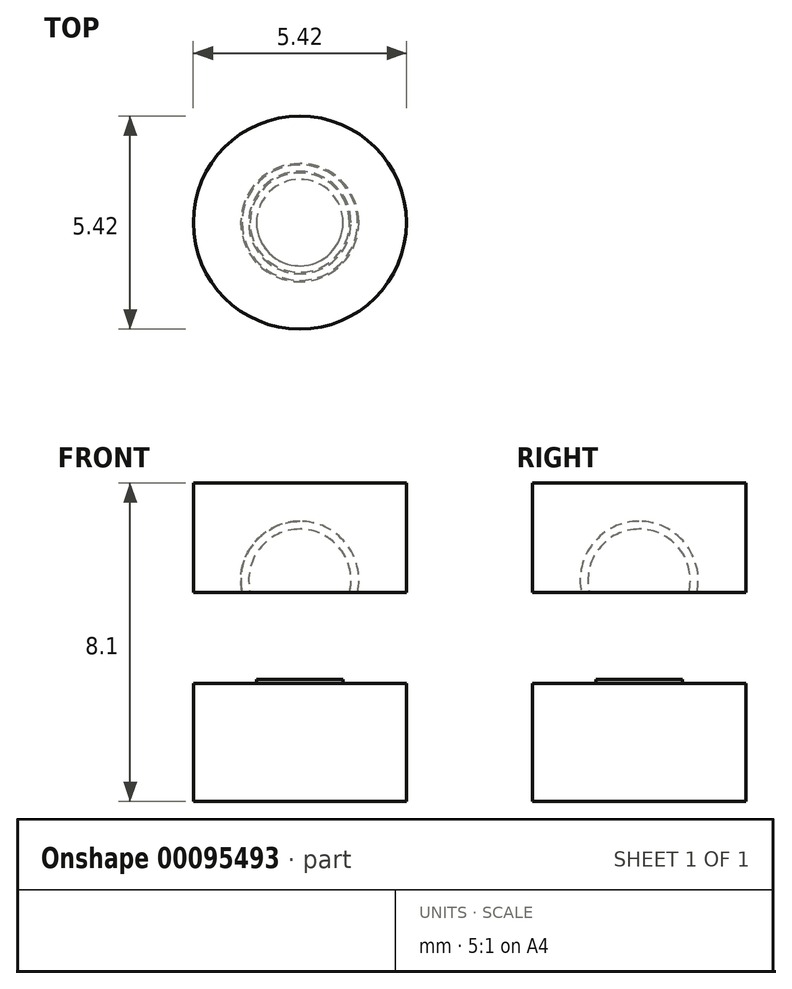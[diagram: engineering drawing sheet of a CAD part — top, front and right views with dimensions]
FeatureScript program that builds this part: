
annotation { "Feature Type Name" : "Feature", "Feature Type Description" : "" }
export const myFeature = defineFeature(function(context is Context, id is Id, definition is map)
    precondition{}
    {
        {
            var Q0;
            Q0=qCreatedBy(makeId("Front.planeOp"),FACE);
            var sketch = newSketch(context, id + "F0", { "sketchPlane" : qUnion([Q0])});
            skArc(sketch, "E0", {"start": v(0, 4.02) * mm, "mid": v(-1.3, 3.27) * mm, "end": v(-1.3, 1.77) * mm});
            skLineSegment(sketch, "E1.bottom", {"start": v(0, 5) * mm, "end": v(-2.7, 5) * mm});
            skLineSegment(sketch, "E1.right", {"start": v(-2.7, 5) * mm, "end": v(-2.7, 0) * mm});
            skPoint(sketch, "E1.middle", {"position": v(0, 0) * mm});
            skLineSegment(sketch, "E2", {"start": v(-1.3, 1.77) * mm, "end": v(-1.3, 0) * mm});
            skPoint(sketch, "E2.endSnap0", {"position": v(2.7, 0) * mm});
            skLineSegment(sketch, "E3", {"start": v(0, 5) * mm, "end": v(0, 4.02) * mm});
            skPoint(sketch, "E4.orphan", {"position": v(2.7, 5) * mm});
            skPoint(sketch, "E5.orphan", {"position": v(2.7, -5) * mm});
            skLineSegment(sketch, "E6", {"start": v(-2.7, 0) * mm, "end": v(-1.3, 0) * mm});
            skPoint(sketch, "E1.top.end.orphan", {"position": v(-2.7, -5) * mm});
            skPoint(sketch, "E1.top.start.orphan", {"position": v(0, -5) * mm});
            skSolve(sketch);
        }
        {
            var Q0;
            Q0=makeQuery(id+"F0.imprint","IMPRINT",FACE,{"disambiguationData":[TD([[makeQuery(id+"F0.imprint","IMPRINT",EDGE,{"derivedFrom":sQuery(id+"F0.wireOp",EDGE,"E0")}),-1.0]])]});
            var Q1;
            Q1=sQuery(id+"F0.wireOp",EDGE,"E3");
            revolve(context, id + "F1", {"entities" : qUnion([Q0]), "axis" : qUnion([Q1]), "revolveType" : RevolveType.FULL});
        }
        {
            var Q0;
            Q0=qCreatedBy(makeId("Front.planeOp"),FACE);
            var sketch = newSketch(context, id + "F2", { "sketchPlane" : qUnion([Q0])});
            skLineSegment(sketch, "E7.0", {"start": v(-1.1, 1.83) * mm, "end": v(-1.1, -0.1) * mm});
            skArc(sketch, "E7.1", {"start": v(0, 3.82) * mm, "mid": v(-1.14, 3.15) * mm, "end": v(-1.1, 1.83) * mm});
            skLineSegment(sketch, "E8.top", {"start": v(-2.7, -3.1) * mm, "end": v(0, -3.1) * mm});
            skLineSegment(sketch, "E8.right", {"start": v(0, 0.26) * mm, "end": v(0, -3.1) * mm});
            skLineSegment(sketch, "E9", {"start": v(0, 3.82) * mm, "end": v(0, -3.1) * mm});
            skLineSegment(sketch, "E10", {"start": v(-2.7, -3.1) * mm, "end": v(-2.7, -0.1) * mm});
            skLineSegment(sketch, "E11", {"start": v(-2.7, -0.1) * mm, "end": v(-1.1, -0.1) * mm});
            skSolve(sketch);
        }
        {
            var Q0;
            Q0=makeQuery(id+"F2.imprint","IMPRINT",FACE,{"disambiguationData":[TD([[makeQuery(id+"F2.imprint","IMPRINT",EDGE,{"derivedFrom":sQuery(id+"F2.wireOp",EDGE,"E7.0")}),1.0]])]});
            var Q1;
            Q1=sQuery(id+"F2.wireOp",EDGE,"E9");
            revolve(context, id + "F3", {"entities" : qUnion([Q0]), "axis" : qUnion([Q1]), "revolveType" : RevolveType.FULL});
        }
        {
            var Q0;
            Q0=qCreatedBy(makeId("Front.planeOp"),FACE);
            var sketch = newSketch(context, id + "F4", { "sketchPlane" : qUnion([Q0])});
            skLineSegment(sketch, "E12", {"start": v(-1.5, 2.2) * mm, "end": v(-2.73, 2.2) * mm});
            skLineSegment(sketch, "E13", {"start": v(-2.73, 2.2) * mm, "end": v(-2.73, 0) * mm});
            skLineSegment(sketch, "E14", {"start": v(-2.73, 0) * mm, "end": v(0, 0) * mm});
            skLineSegment(sketch, "E15", {"start": v(0, 0) * mm, "end": v(0, 2.2) * mm});
            skLineSegment(sketch, "E16", {"start": v(0, 2.2) * mm, "end": v(-1.5, 2.2) * mm});
            skSolve(sketch);
        }
        {
            var Q0;
            Q0 = qSketchRegion(id + "F4", true);
            var Q1;
            Q1=makeQuery(id+"F1.opRevolve","SWEPT_FACE",FACE,{"disambiguationData":[OSD([sQuery(id+"F0.wireOp",EDGE,"E1.right")])]});
            revolve(context, id + "F5", {"operationType" : NewBodyOperationType.REMOVE, "entities" : qUnion([Q0]), "axis" : qUnion([Q1]), "revolveType" : RevolveType.FULL, "oppositeDirection" : true});
        }
    });
